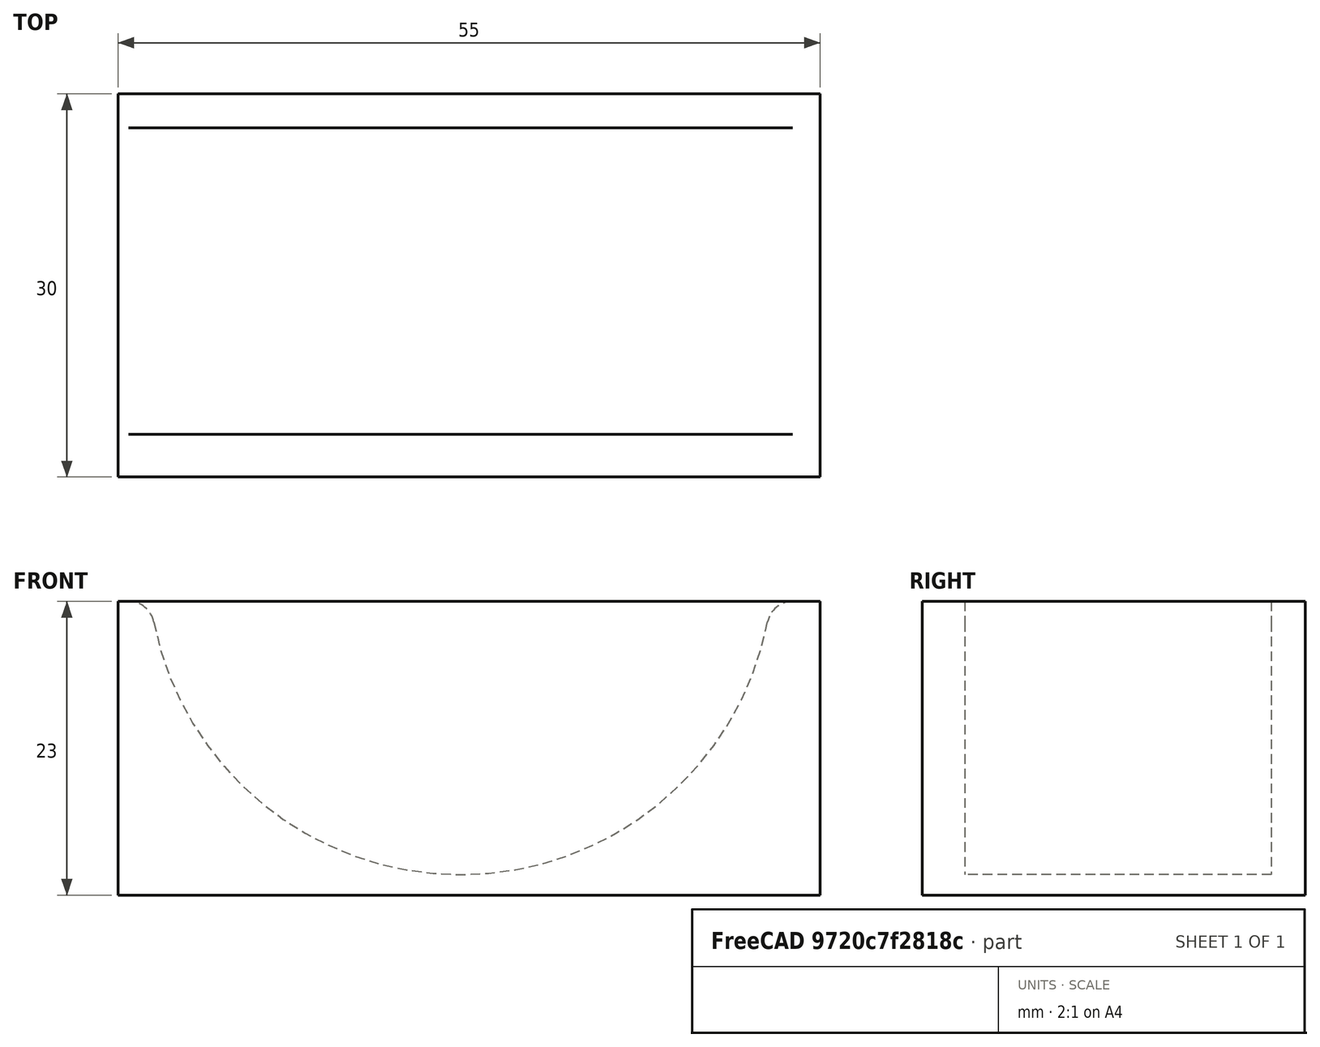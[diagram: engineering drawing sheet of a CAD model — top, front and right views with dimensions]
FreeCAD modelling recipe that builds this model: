
FCSTD DOCUMENT  (FreeCAD 1.1R20260325 (Git shallow))
Label: gridfinity-wire-bin
License: All rights reserved
objects: App::Point×3, App::Link×2, App::FeaturePython×2, PartDesign::SubShapeBinder×2, Assembly::JointGroup×1, Assembly::AssemblyObject×1, Part::FeaturePython×1, PartDesign::FeatureBase×1, Sketcher::SketchObject×1, App::VarSet×1, PartDesign::Pocket×1, PartDesign::Fillet×1, Part::DatumPoint×1, Part::DatumPlane×1, PartDesign::Mirrored×1, PartDesign::LinearPattern×1, PartDesign::MultiTransform×1, PartDesign::Body×1, Part::Box×1, Part::MultiCommon×1, +1 more types
note: 22 computed .brp shape members not serialized (recipe doc carries the construction recipe); baked Part::Feature solids carry a one-line shape summary decoded from their .brp
EXTERNAL_REF file=wire-rolls.FCStd obj=Body

FEATURE [App::Point] Origin001
  Role = Origin
FEATURE [App::Link] wire_role_half  label="wire-role-half"
  LinkedObject = -> <external wire-rolls.FCStd>#Body
FEATURE [App::FeaturePython] GroundedJoint  # Assembly grounded joint (typed FeaturePython)
  ObjectToGround = -> wire_role_half
FEATURE [App::Link] wire_role_half001  label="wire-role-half001"
  LinkPlacement = pos=(0,0,23) rot=(0,1,0;3.14159rad)
  LinkedObject = -> <external wire-rolls.FCStd>#Body
  Placement = pos=(0,0,23) rot=(0,1,0;3.14159rad)
FEATURE [App::FeaturePython] Joint  label="Fixed"  # Assembly joint (typed FeaturePython)
  Angle = 0
  AngleMax = 0
  AngleMin = 0
  Detach1 = false
  Detach2 = false
  Distance = 0
  Distance2 = 0
  EnableAngleMax = false
  EnableAngleMin = false
  EnableLengthMax = false
  EnableLengthMin = false
  JointType = 0 (Fixed)
  LengthMax = 0
  LengthMin = 0
  Offset2 = pos=(0,0,0) rot=(0,0,1;3.14159rad)
  Placement1 = pos=(0,0,11.5) rot=(0,0,1;0rad)
  Placement2 = pos=(0,0,11.5) rot=(0,0,1;3.14159rad)
  Reference1 = -> wire_role_half001 [Edge43,Edge43]
  Reference2 = -> wire_role_half [Face14,Edge1]
  Suppressed = false
FEATURE [Assembly::JointGroup] Joints
  Group = -> [GroundedJoint,Joint]
FEATURE [Assembly::AssemblyObject] Assembly  label="spool"
  Group = -> [Joints,wire_role_half,GroundedJoint,wire_role_half001,Joint]
  Origin = -> Origin
  Placement = pos=(32.85,95.15,3.105) rot=(-1,0,0;1.5708rad)
  Type = Assembly
FEATURE [Part::FeaturePython] BinBlank  # WARN: FeaturePython — macro-defined, semantics opaque (R4)
  BaseProfileBottomChamfer = 0.8
  BaseProfileHeight = 4.75
  BaseProfileTopChamfer = 2.15
  BaseProfileVerticalSection = 1.8
  Baseplate = false
  BinBottomRadius = 0.8
  BinOuterRadius = 3.75
  BinVerticalRadius = 1.6
  Clearance = 0.25
  CrushRibsCount = 12
  CrushRibsWaviness = 0.5
  CustomHeight = 42
  GenerationLocation = 0
  HeightUnitValue = 7
  HeightUnits = 4
  MagnetHoleDepth = 2.4
  MagnetHoleDiameter = 6.2
  MagnetHoleDistanceFromEdge = 8
  MagnetHoles = false
  MagnetHolesShape = 0
  MagnetRemoveChannel = false
  NonStandardHeight = false
  RecessedTopDepth = 0
  ScrewHoleDepth = 6
  ScrewHoleDiameter = 3
  ScrewHoles = false
  SequentialBridgingLayerHeight = 0.2
  StackingLip = true
  StackingLipBottomChamfer = 0.7
  StackingLipTopChamfer = 1.5
  StackingLipTopLedge = 0.4
  StackingLipVerticalSection = 1.8
  TotalHeight = 28
  WallThickness = 1
  version = 0.12.0
  xGridSize = 42
  xGridUnits = 3
  xLocationOffset = 0
  xTotalWidth = 125.5
  yGridSize = 42
  yGridUnits = 3
  yLocationOffset = 0
  yTotalWidth = 125.5
  expr: BaseProfileHeight = BaseProfileBottomChamfer + BaseProfileVerticalSection + BaseProfileTopChamfer
  expr: TotalHeight = NonStandardHeight == 1 ? CustomHeight : HeightUnits * HeightUnitValue
  expr: xTotalWidth = xGridUnits * xGridSize - (Baseplate == 1 ? 0 mm : 2 * Clearance)
  expr: yTotalWidth = yGridUnits * yGridSize - (Baseplate == 1 ? 0 mm : 2 * Clearance)
FEATURE [App::Point] Origin003
  Role = Origin
FEATURE [PartDesign::FeatureBase] BaseFeature
  BaseFeature = -> BinBlank
  Suppressed = false
FEATURE [PartDesign::SubShapeBinder] Binder  label="sides-spool-ref"
  BindCopyOnChange = 0
  BindMode = 0
  ClaimChildren = false
  Context = -> Part [Body.Binder.]
  Fuse = false
  MakeFace = true
  OffsetFill = false
  OffsetIntersection = false
  OffsetJoinType = 0
  OffsetOpenResult = false
  PartialLoad = false
  Refine = true
  Relative = true
  Support = -> [Assembly[wire_role_half.Chamfer001.Face1,wire_role_half001.Chamfer001.Face1]]
  _Version = 2
FEATURE [PartDesign::SubShapeBinder] Binder001  label="spool-radius-ref"
  BindCopyOnChange = 0
  BindMode = 0
  ClaimChildren = false
  Context = -> Part [Body.Binder001.]
  Fuse = false
  MakeFace = true
  OffsetFill = false
  OffsetIntersection = false
  OffsetJoinType = 0
  OffsetOpenResult = false
  PartialLoad = false
  Refine = true
  Relative = true
  Support = -> [Assembly[wire_role_half.Chamfer001.Edge17]]
  _Version = 2
FEATURE [Sketcher::SketchObject] Sketch  label="cut-out-profile"
  ArcFitTolerance = 1e-06
  AttachmentOffset = pos=(0,0,0.5) rot=(0,0,1;0rad)
  AttachmentSupport = -> [Binder]
  ExternalGeometry = -> [Binder001]
  ExternalTypes = [0]
  FullyConstrained = true
  MakeInternals = false
  MapMode = 5
  Placement = pos=(0,94.65,2.12e-14) rot=(1,0,0;1.5708rad)
  _ExternalGeoVersion = 1
  expr: .AttachmentOffset.Base.z = VarSet.clearance
  expr: Constraints[1] = VarSet.clearance
  sketch-geometry (1):
    g0: Circle CenterX=32.85 CenterY=3.105 CenterZ=0 NormalX=0 NormalY=0 NormalZ=1 AngleXU=0 Radius=24.5
  constraints (2):
    c: Coincident(g0,g-3)
    c: Distance(g-3,g0) = 0.5
FEATURE [App::VarSet] VarSet
  SideDistance = 5
  clearance = 0.5
  gap = 0.2
FEATURE [PartDesign::Pocket] Pocket  label="cut-out-1"
  BaseFeature = -> BaseFeature
  Direction = (0,1,-2e-16)
  Length = 5
  Length2 = 5
  Offset = -0.5
  Profile = -> Sketch
  ReferenceAxis = -> Sketch [N_Axis]
  SideType = 0
  Suppressed = false
  Type = 3
  Type2 = 0
  UpToFace = -> Binder [Face2]
  expr: Offset = VarSet.clearance * -1
FEATURE [PartDesign::Fillet] Fillet  label="roll-out-fillets"
  Base = -> Pocket [Edge600,Edge602]
  BaseFeature = -> Pocket
  Radius = 2
  SupportTransform = false
  Suppressed = false
  UseAllEdges = false
FEATURE [Part::DatumPoint] DatumPoint  label="mid-point"
  AttacherType = Attacher::AttachEnginePoint
  AttachmentSupport = -> [Fillet]
  MapMode = 37
  Placement = pos=(63,123.85,2.5) rot=(0,0,1;0rad)
FEATURE [Part::DatumPlane] DatumPlane  label="mid-plane"
  AttachmentSupport = -> [DatumPoint]
  MapMode = 4
  Placement = pos=(63,123.85,2.5) rot=(0.57735,0.57735,0.57735;2.0944rad)
FEATURE [PartDesign::Mirrored] Mirror
  MirrorPlane = -> DatumPlane
  Suppressed = false
  TransformMode = 0
FEATURE [PartDesign::LinearPattern] Linear_Pattern
  Direction = -> Y_Axis001
  Direction2 = -> X_Axis001
  Length = 87.3
  Length2 = 100
  Mode = 1
  Mode2 = 0
  Occurrences = 4
  Occurrences2 = 1
  Offset = 29.1
  Offset2 = 100
  Reversed = true
  Reversed2 = false
  SpacingPattern = [0]
  SpacingPattern2 = [0]
  Spacings = [-1,-1,-1]
  Suppressed = false
  TransformMode = 0
FEATURE [PartDesign::MultiTransform] MultiTransform
  BaseFeature = -> Fillet
  Originals = -> [Fillet,Pocket]
  Suppressed = false
  TransformMode = 0
  Transformations = -> [Mirror,Linear_Pattern]
FEATURE [PartDesign::Body] Body  label="gridfinity-spool-holder"
  AllowCompound = false
  BaseFeature = -> BinBlank
  Group = -> [BaseFeature,Binder,Binder001,Sketch,VarSet,Pocket,Fillet,DatumPoint,DatumPlane,MultiTransform,Mirror,Linear_Pattern]
  Origin = -> Origin002
  Tip = -> MultiTransform
FEATURE [Part::Box] Box  label="Cube"
  AttacherType = Attacher::AttachEngine3D
  Height = 24
  Length = 55
  Placement = pos=(6,4,-23) rot=(0,0,1;0rad)
  Width = 30
FEATURE [Part::MultiCommon] Common
  Behavior = 0
  Shapes = -> [Box,Body]
FEATURE [App::Point] Origin005  label="Origin006"
  Role = Origin
FEATURE [App::Part] Part  label="test"
  Group = -> [Box,BinBlank,Body,Common]
  Origin = -> Origin004
